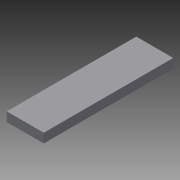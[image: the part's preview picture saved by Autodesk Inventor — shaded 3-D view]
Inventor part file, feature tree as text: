
AUTODESK INVENTOR PART (.ipt)
format: ipt  version: 2014 (Build 180170000, 170)  size: 68,096 bytes
history: native  units: in
note: dims shown in document units (in); Inventor stores cm internally (conversion verified against a paired STEP export)
features: extrude x1, sketch x1
ambient origin geometry x8: Origin, YZ Plane, XZ Plane, XY Plane, X Axis, Y Axis, Z Axis, Center Point
bodies: Solid1 (feature_tree)
feature tree (2):
  extrude  "Extrusion1"  Depth=1.0in
  sketch  "Sketch1"  dims[d0=3.5in d1=1.0in d2=0.25in d3=0.0in]
